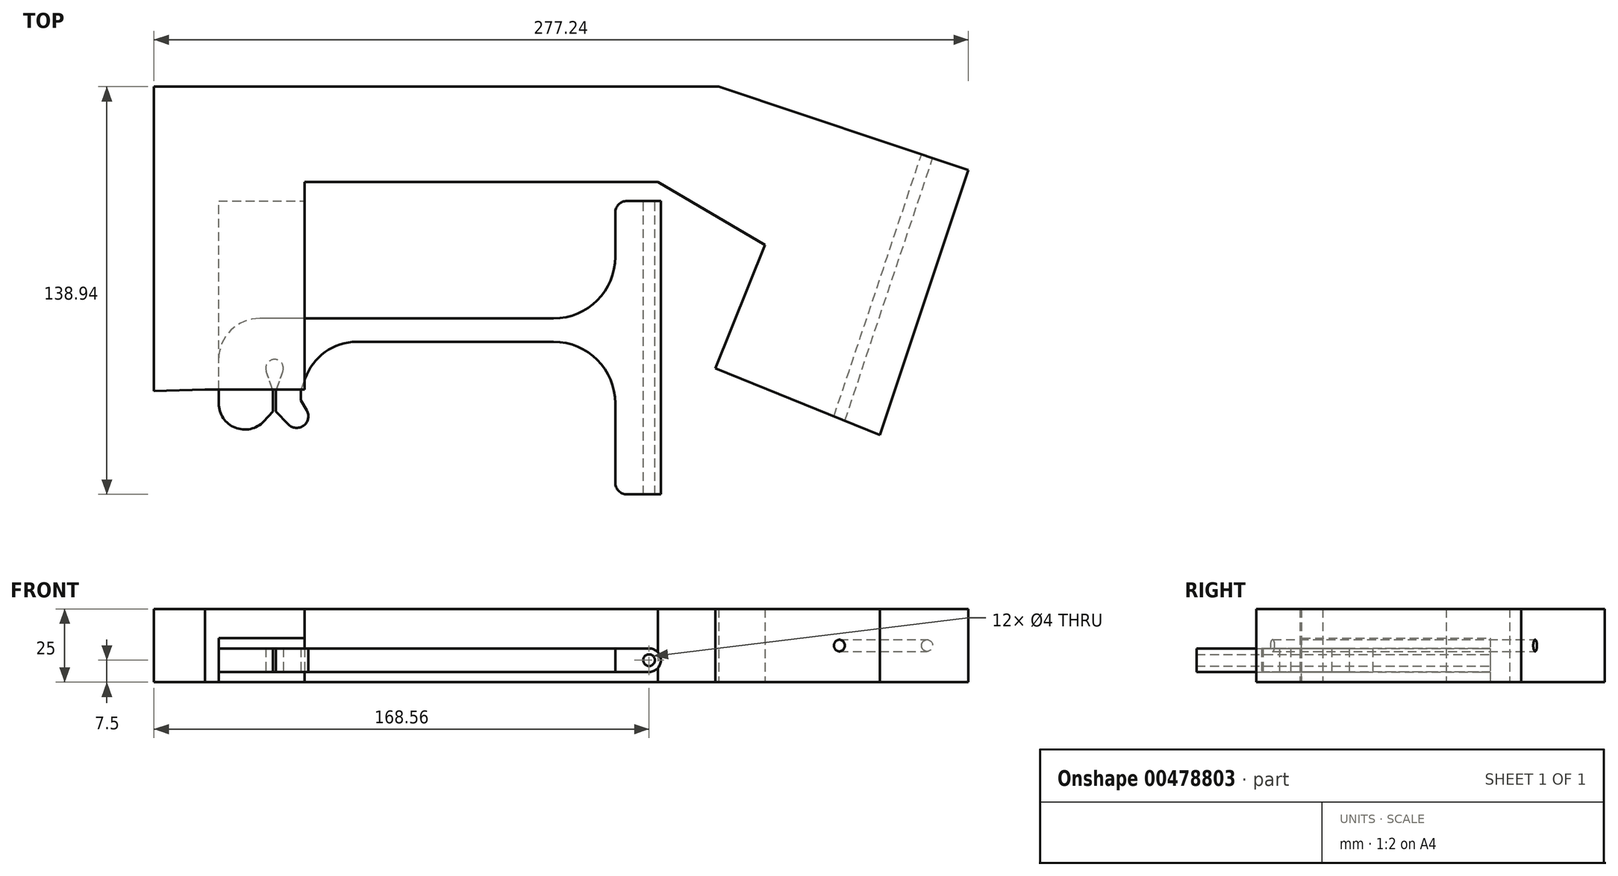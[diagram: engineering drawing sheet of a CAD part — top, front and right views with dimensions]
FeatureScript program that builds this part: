
annotation { "Feature Type Name" : "Feature", "Feature Type Description" : "" }
export const myFeature = defineFeature(function(context is Context, id is Id, definition is map)
    precondition{}
    {
        {
            var Q0;
            Q0=qCreatedBy(makeId("Top.planeOp"),FACE);
            var sketch = newSketch(context, id + "F0", { "sketchPlane" : qUnion([Q0])});
            skLineSegment(sketch, "E0", {"start": v(0, 0) * mm, "end": v(-2.07, 2.07) * mm});
            skLineSegment(sketch, "E1", {"start": v(-7.07, 7.07) * mm, "end": v(-7.07, 27.07) * mm, "construction": true});
            skLineSegment(sketch, "E2", {"start": v(-7.07, 7.07) * mm, "end": v(-12.07, 2.07) * mm, "construction": true});
            skLineSegment(sketch, "E3", {"start": v(-7.07, 27.07) * mm, "end": v(-2.07, 29.96) * mm, "construction": true});
            skLineSegment(sketch, "E4", {"start": v(-7.07, 27.07) * mm, "end": v(-12.07, 29.96) * mm, "construction": true});
            skArc(sketch, "E5", {"start": v(-12.07, 29.96) * mm, "mid": v(-7.07, 48.62) * mm, "end": v(-2.07, 29.96) * mm});
            skLineSegment(sketch, "E6.0", {"start": v(-2.07, 2.07) * mm, "end": v(-2.07, 29.96) * mm});
            skLineSegment(sketch, "E7.0", {"start": v(-12.07, 2.07) * mm, "end": v(-12.07, 29.96) * mm});
            skLineSegment(sketch, "E8", {"start": v(-12.07, 29.96) * mm, "end": v(-12.07, 29.96) * mm});
            skLineSegment(sketch, "E9", {"start": v(-2.07, 29.96) * mm, "end": v(-2.07, 29.96) * mm});
            skLineSegment(sketch, "E10", {"start": v(-12.07, 2.07) * mm, "end": v(-14.14, 0) * mm});
            skLineSegment(sketch, "E11", {"start": v(-2.07, 2.07) * mm, "end": v(-7.07, 7.07) * mm, "construction": true});
            skLineSegment(sketch, "E12", {"start": v(-14.14, 0) * mm, "end": v(-24.14, 0) * mm});
            skLineSegment(sketch, "E13", {"start": v(-24.14, 0) * mm, "end": v(-24.14, 60) * mm});
            skLineSegment(sketch, "E14", {"start": v(-24.14, 60) * mm, "end": v(175.86, 60) * mm});
            skLineSegment(sketch, "E15", {"start": v(175.86, 60) * mm, "end": v(175.86, 0) * mm});
            skLineSegment(sketch, "E16.bottom", {"start": v(-17.07, 48.62) * mm, "end": v(2.93, 48.62) * mm});
            skLineSegment(sketch, "E16.top", {"start": v(-17.07, 28.62) * mm, "end": v(2.93, 28.62) * mm});
            skLineSegment(sketch, "E16.left", {"start": v(-17.07, 48.62) * mm, "end": v(-17.07, 28.62) * mm});
            skLineSegment(sketch, "E16.right", {"start": v(2.93, 48.62) * mm, "end": v(2.93, 28.62) * mm});
            skFitSpline(sketch, "E17", {"points": [v(0, 0) * mm, v(-2.07, 2.07) * mm, v(-2.07, 29.96) * mm, v(2.93, 38.62) * mm, v(2.93, 48.62) * mm, v(-17.07, 48.62) * mm, v(-17.07, 38.62) * mm, v(-12.07, 29.96) * mm, v(-12.07, 2.07) * mm, v(-14.14, 0) * mm, v(-24.14, 60) * mm, v(175.86, 60) * mm, v(175.86, 0) * mm], "startDerivative": vector(-121.96, 63.14) * mm, "endDerivative": vector(-229.47, -514.3) * mm});
            skSolve(sketch);
        }
        {
            var Q0;
            Q0=sQuery(id+"F0.wireOp",EDGE,"E17");
            extrude(context, id + "F1", {"bodyType" : ToolBodyType.SURFACE, "surfaceEntities" : qUnion([Q0]), "depth" : 25 * mm});
        }
        {
            var Q0;
            Q0=qCreatedBy(makeId("Top.planeOp"),FACE);
            var sketch = newSketch(context, id + "F2", { "sketchPlane" : qUnion([Q0])});
            skLineSegment(sketch, "E18", {"start": v(-23.73, -7.24) * mm, "end": v(10.25, -7.24) * mm});
            skLineSegment(sketch, "E19", {"start": v(10.25, -7.24) * mm, "end": v(10.25, 63.52) * mm});
            skLineSegment(sketch, "E20", {"start": v(10.25, 63.52) * mm, "end": v(130.47, 63.52) * mm});
            skLineSegment(sketch, "E21", {"start": v(130.47, 63.52) * mm, "end": v(166.99, 41.96) * mm});
            skLineSegment(sketch, "E22", {"start": v(166.99, 41.96) * mm, "end": v(150, 0) * mm});
            skLineSegment(sketch, "E23", {"start": v(150, 0) * mm, "end": v(206.05, -22.7) * mm});
            skLineSegment(sketch, "E24", {"start": v(206.05, -22.7) * mm, "end": v(236.18, 67.57) * mm});
            skLineSegment(sketch, "E25", {"start": v(236.18, 67.57) * mm, "end": v(151.2, 95.94) * mm});
            skLineSegment(sketch, "E26", {"start": v(151.2, 95.94) * mm, "end": v(-41.06, 95.94) * mm});
            skLineSegment(sketch, "E27", {"start": v(-41.06, 95.94) * mm, "end": v(-41.06, -7.75) * mm});
            skLineSegment(sketch, "E28", {"start": v(-41.06, -7.75) * mm, "end": v(-23.73, -7.24) * mm});
            skSolve(sketch);
        }
        {
            var Q0;
            Q0=makeQuery(id+"F2.imprint","IMPRINT",FACE,{"disambiguationData":[TD([[makeQuery(id+"F2.imprint","IMPRINT",EDGE,{"derivedFrom":sQuery(id+"F2.wireOp",EDGE,"E18")}),1.0]])]});
            extrude(context, id + "F3", {"entities" : qUnion([Q0]), "depth" : 25 * mm});
        }
        {
            var Q0;
            Q0=makeQuery(id+"F3.opExtrude","SWEPT_FACE",FACE,{"disambiguationData":[OSD([sQuery(id+"F2.wireOp",EDGE,"E25")])]});
            var sketch = newSketch(context, id + "F4", { "sketchPlane" : qUnion([Q0])});
            skLineSegment(sketch, "E29.0.0", {"start": v(-202.64, 0) * mm, "end": v(-113.04, 0) * mm});
            skLineSegment(sketch, "E29.0.1", {"start": v(-113.04, 0) * mm, "end": v(-113.04, 25) * mm});
            skLineSegment(sketch, "E29.0.2", {"start": v(-113.04, 25) * mm, "end": v(-202.64, 25) * mm});
            skLineSegment(sketch, "E29.0.3", {"start": v(-202.64, 25) * mm, "end": v(-202.64, 0) * mm});
            skCircle(sketch, "E30", {"center": v(-187.81, 12.5) * mm, "radius": 2 * mm});
            skPoint(sketch, "E30.centerSnap0", {"position": v(-202.64, 12.5) * mm});
            skSolve(sketch);
        }
        {
            var Q0;
            Q0=makeQuery(id+"F4.imprint","IMPRINT",FACE,{"disambiguationData":[TD([[makeQuery(id+"F4.imprint","IMPRINT",EDGE,{"derivedFrom":sQuery(id+"F4.wireOp",EDGE,"E30")}),1.0]])]});
            var Q1;
            Q1=makeQuery(id+"F3.opExtrude","SWEPT_FACE",FACE,{"disambiguationData":[OSD([sQuery(id+"F2.wireOp",EDGE,"E23")])]});
            extrude(context, id + "F5", {"entities" : qUnion([Q0]), "operationType" : NewBodyOperationType.REMOVE, "endBound" : BoundingType.UP_TO_SURFACE, "oppositeDirection" : true, "endBoundEntityFace" : qUnion([Q1]), "depth" : 25 * mm});
        }
        {
            var Q0;
            Q0=qCreatedBy(makeId("Top.planeOp"),FACE);
            var sketch = newSketch(context, id + "F6", { "sketchPlane" : qUnion([Q0])});
            skArc(sketch, "E31", {"start": v(6.62, -2.27) * mm, "mid": v(0, 7) * mm, "end": v(-6.62, -2.27) * mm});
            skLineSegment(sketch, "E32", {"start": v(6.62, -2.27) * mm, "end": v(5, -7) * mm});
            skLineSegment(sketch, "E33", {"start": v(5, -7) * mm, "end": v(5, -12) * mm});
            skLineSegment(sketch, "E34", {"start": v(5, -12) * mm, "end": v(7.5, -16.33) * mm});
            skLineSegment(sketch, "E35.MirrorCS", {"start": v(-6.62, -2.27) * mm, "end": v(-5, -7) * mm});
            skLineSegment(sketch, "E36.MirrorCS", {"start": v(-5, -7) * mm, "end": v(-5, -12) * mm});
            skLineSegment(sketch, "E37.MirrorCS", {"start": v(-5, -12) * mm, "end": v(-7.5, -16.33) * mm});
            skLineSegment(sketch, "E38.2", {"start": v(-2.84, -0.97) * mm, "end": v(-0.5, -7.8) * mm});
            skLineSegment(sketch, "E38.5", {"start": v(2.84, -0.97) * mm, "end": v(0.5, -7.8) * mm});
            skArc(sketch, "E38.6", {"start": v(2.84, -0.97) * mm, "mid": v(0, 3) * mm, "end": v(-2.84, -0.97) * mm});
            skArc(sketch, "E39", {"start": v(-10.96, -14.33) * mm, "mid": v(-9.9, -19.53) * mm, "end": v(-4.6, -19.09) * mm, "construction": true});
            skArc(sketch, "E40.MirrorCS", {"start": v(10.96, -14.33) * mm, "mid": v(9.9, -19.53) * mm, "end": v(4.6, -19.09) * mm});
            skLineSegment(sketch, "E41.0", {"start": v(9, -10.93) * mm, "end": v(10.96, -14.33) * mm});
            skLineSegment(sketch, "E41.1", {"start": v(9, -7.67) * mm, "end": v(9, -10.93) * mm});
            skLineSegment(sketch, "E41.2", {"start": v(10.4, -3.57) * mm, "end": v(9, -7.67) * mm});
            skLineSegment(sketch, "E41.3", {"start": v(-9, -10.93) * mm, "end": v(-10.96, -14.33) * mm, "construction": true});
            skLineSegment(sketch, "E41.4", {"start": v(-9, -7.67) * mm, "end": v(-9, -10.93) * mm, "construction": true});
            skLineSegment(sketch, "E41.5", {"start": v(-10.4, -3.57) * mm, "end": v(-9, -7.67) * mm, "construction": true});
            skArc(sketch, "E41.6", {"start": v(10.4, -3.57) * mm, "mid": v(0, 11) * mm, "end": v(-10.4, -3.57) * mm, "construction": true});
            skPoint(sketch, "E42.orphan", {"position": v(-5.5, -12.87) * mm});
            skPoint(sketch, "E43.orphan", {"position": v(5.5, -12.87) * mm});
            skLineSegment(sketch, "E44", {"start": v(0, 0) * mm, "end": v(0, -13.5) * mm, "construction": true});
            skLineSegment(sketch, "E45", {"start": v(0, -9.25) * mm, "end": v(0, -14.25) * mm, "construction": true});
            skLineSegment(sketch, "E46", {"start": v(0, -14.25) * mm, "end": v(-0.5, -14.78) * mm, "construction": true});
            skLineSegment(sketch, "E47", {"start": v(0, -14.25) * mm, "end": v(0.5, -14.78) * mm, "construction": true});
            skLineSegment(sketch, "E48", {"start": v(-7.5, -16.33) * mm, "end": v(-12.5, -16.33) * mm});
            skLineSegment(sketch, "E49", {"start": v(-12.5, -16.33) * mm, "end": v(-15, -12) * mm});
            skLineSegment(sketch, "E50", {"start": v(-15, -12) * mm, "end": v(-15, 3) * mm});
            skArc(sketch, "E51", {"start": v(-15, 3) * mm, "mid": v(-12.07, 10.07) * mm, "end": v(-5, 13) * mm});
            skLineSegment(sketch, "E52", {"start": v(-5, 13) * mm, "end": v(95, 13) * mm});
            skArc(sketch, "E53", {"start": v(95, 13) * mm, "mid": v(112.68, 5.68) * mm, "end": v(120, -12) * mm});
            skLineSegment(sketch, "E54", {"start": v(120, -12) * mm, "end": v(120, -39) * mm});
            skLineSegment(sketch, "E55.0", {"start": v(124, -12) * mm, "end": v(124, -39) * mm});
            skLineSegment(sketch, "E55.1", {"start": v(-19, -12) * mm, "end": v(-19, 3) * mm});
            skArc(sketch, "E55.2", {"start": v(-19, 3) * mm, "mid": v(-14.9, 12.9) * mm, "end": v(-5, 17) * mm});
            skLineSegment(sketch, "E55.3", {"start": v(-5, 17) * mm, "end": v(95, 17) * mm});
            skArc(sketch, "E55.4", {"start": v(95, 17) * mm, "mid": v(115.5, 8.5) * mm, "end": v(124, -12) * mm});
            skLineSegment(sketch, "E56.0", {"start": v(116, -12) * mm, "end": v(116, -39) * mm});
            skArc(sketch, "E56.1", {"start": v(95, 9) * mm, "mid": v(109.85, 2.85) * mm, "end": v(116, -12) * mm});
            skLineSegment(sketch, "E56.2", {"start": v(-5, 9) * mm, "end": v(95, 9) * mm});
            skArc(sketch, "E57", {"start": v(116, -39) * mm, "mid": v(120, -43) * mm, "end": v(124, -39) * mm});
            skLineSegment(sketch, "E58", {"start": v(120, -43) * mm, "end": v(135, -43) * mm});
            skPoint(sketch, "E58.endSnap0", {"position": v(120, -43) * mm});
            skLineSegment(sketch, "E59", {"start": v(135, -43) * mm, "end": v(135, 17) * mm});
            skLineSegment(sketch, "E60", {"start": v(135, 17) * mm, "end": v(124, 17) * mm});
            skLineSegment(sketch, "E61", {"start": v(124, 17) * mm, "end": v(95, 17) * mm});
            skArc(sketch, "E62", {"start": v(-19, -12) * mm, "mid": v(-13.41, -20.25) * mm, "end": v(-3.68, -18.12) * mm});
            skLineSegment(sketch, "E63", {"start": v(-3.68, -18.12) * mm, "end": v(-4.6, -19.09) * mm, "construction": true});
            skArc(sketch, "E64", {"start": v(28, 9) * mm, "mid": v(17.19, 5.54) * mm, "end": v(10.4, -3.57) * mm});
            skLineSegment(sketch, "E65", {"start": v(-0.5, -14.78) * mm, "end": v(-0.5, -7.8) * mm});
            skLineSegment(sketch, "E66.MirrorCS", {"start": v(0.5, -14.78) * mm, "end": v(0.5, -7.8) * mm});
            skLineSegment(sketch, "E67", {"start": v(-0.5, -7.8) * mm, "end": v(0, -9.25) * mm, "construction": true});
            skLineSegment(sketch, "E68", {"start": v(0.5, -7.8) * mm, "end": v(0, -9.25) * mm, "construction": true});
            skLineSegment(sketch, "E69", {"start": v(-0.5, -14.78) * mm, "end": v(-3.68, -18.12) * mm});
            skLineSegment(sketch, "E70", {"start": v(0.5, -14.78) * mm, "end": v(4.6, -19.09) * mm});
            skArc(sketch, "E71", {"start": v(95, 13) * mm, "mid": v(112.68, 20.32) * mm, "end": v(120, 38) * mm});
            skArc(sketch, "E72.0", {"start": v(95, 17) * mm, "mid": v(109.85, 23.15) * mm, "end": v(116, 38) * mm});
            skLineSegment(sketch, "E73", {"start": v(135, 17) * mm, "end": v(135, 57) * mm});
            skArc(sketch, "E74", {"start": v(120, 57) * mm, "mid": v(117.17, 55.83) * mm, "end": v(116, 53) * mm});
            skLineSegment(sketch, "E75", {"start": v(116, 38) * mm, "end": v(116, 53) * mm});
            skLineSegment(sketch, "E76", {"start": v(120, 57) * mm, "end": v(135, 57) * mm});
            skSolve(sketch);
        }
        {
            var Q0;
            {var subQ1=sQuery(id+"F6.wireOp",EDGE,"E55.0");Q0=makeQuery(id+"F6.imprint","IMPRINT",FACE,{"disambiguationData":[TD([[makeQuery(id+"F6.imprint","IMPRINT",EDGE,{"derivedFrom":subQ1}),1.0]])]});}
            var Q1;
            Q1=makeQuery(id+"F6.imprint","IMPRINT",FACE,{"disambiguationData":[TD([[makeQuery(id+"F6.imprint","IMPRINT",EDGE,{"derivedFrom":sQuery(id+"F6.wireOp",EDGE,"E38.2")}),-1.0]])]});
            var Q2;
            {var subQ3=sQuery(id+"F6.wireOp",EDGE,"E60");Q2=makeQuery(id+"F6.imprint","IMPRINT",FACE,{"disambiguationData":[TD([[makeQuery(id+"F6.imprint","IMPRINT",EDGE,{"derivedFrom":subQ3}),-1.0]])]});}
            var Q3;
            {var subQ1=sQuery(id+"F6.wireOp",EDGE,"E55.4");var subQ3=sQuery(id+"F6.wireOp",EDGE,"E71");var subQ4=makeQuery(id+"F6.imprint","INTERSECT",VERTEX,{"derivedFrom":[subQ1,subQ3]});Q3=makeQuery(id+"F6.imprint","IMPRINT",FACE,{"disambiguationData":[TD([[makeQuery(id+"F6.imprint","IMPRINT",EDGE,{"disambiguationData":[TD([[subQ4,-1.0]])],"derivedFrom":subQ3}),1.0]])]});}
            extrude(context, id + "F7", {"entities" : qUnion([Q0, Q1, Q2, Q3]), "depth" : 15 * mm});
        }
        {
            var Q0;
            Q0=makeQuery(id+"F7.opExtrude","SWEPT_FACE",FACE,{"disambiguationData":[OSD([sQuery(id+"F6.wireOp",EDGE,"E76")])]});
            var sketch = newSketch(context, id + "F8", { "sketchPlane" : qUnion([Q0])});
            skLineSegment(sketch, "E77.0.0", {"start": v(-120, 0) * mm, "end": v(-135, 0) * mm});
            skLineSegment(sketch, "E77.0.1", {"start": v(-135, 0) * mm, "end": v(-135, 15) * mm});
            skLineSegment(sketch, "E77.0.2", {"start": v(-135, 15) * mm, "end": v(-120, 15) * mm});
            skLineSegment(sketch, "E77.0.3", {"start": v(-120, 15) * mm, "end": v(-120, 0) * mm});
            skCircle(sketch, "E78", {"center": v(-127.5, 7.5) * mm, "radius": 2 * mm});
            skLineSegment(sketch, "E79", {"start": v(-127.5, 7.5) * mm, "end": v(-127.5, 15) * mm, "construction": true});
            skLineSegment(sketch, "E80", {"start": v(-127.5, 7.5) * mm, "end": v(-135, 7.5) * mm, "construction": true});
            skSolve(sketch);
        }
        {
            var Q0;
            Q0=makeQuery(id+"F8.imprint","IMPRINT",FACE,{"disambiguationData":[TD([[makeQuery(id+"F8.imprint","IMPRINT",EDGE,{"derivedFrom":sQuery(id+"F8.wireOp",EDGE,"E78")}),1.0]])]});
            extrude(context, id + "F9", {"entities" : qUnion([Q0]), "operationType" : NewBodyOperationType.REMOVE, "endBound" : BoundingType.THROUGH_ALL, "oppositeDirection" : true, "depth" : 25 * mm});
        }
        {
            var Q0;
            Q0=makeQuery(id+"F7.opExtrude","SWEPT_FACE",FACE,{"disambiguationData":[OSD([sQuery(id+"F6.wireOp",EDGE,"E76")])]});
            var sketch = newSketch(context, id + "F10", { "sketchPlane" : qUnion([Q0])});
            skCircle(sketch, "E81", {"center": v(-127.5, 7.5) * mm, "radius": 4 * mm});
            skLineSegment(sketch, "E82.0.0", {"start": v(-95, 0) * mm, "end": v(5, 0) * mm});
            skLineSegment(sketch, "E82.0.1", {"start": v(5, 0) * mm, "end": v(5, 15) * mm});
            skLineSegment(sketch, "E82.0.2", {"start": v(5, 15) * mm, "end": v(-95, 15) * mm});
            skLineSegment(sketch, "E82.0.3", {"start": v(-95, 15) * mm, "end": v(-95, 0) * mm});
            skLineSegment(sketch, "E83.0.0", {"start": v(5, 0) * mm, "end": v(19, 0) * mm});
            skLineSegment(sketch, "E83.0.1", {"start": v(19, 0) * mm, "end": v(19, 15) * mm});
            skLineSegment(sketch, "E83.0.2", {"start": v(19, 15) * mm, "end": v(5, 15) * mm});
            skLineSegment(sketch, "E83.0.3", {"start": v(5, 15) * mm, "end": v(5, 0) * mm});
            skLineSegment(sketch, "E84.0.0", {"start": v(-116, 0) * mm, "end": v(-95, 0) * mm});
            skLineSegment(sketch, "E84.0.1", {"start": v(-95, 0) * mm, "end": v(-95, 15) * mm});
            skLineSegment(sketch, "E84.0.2", {"start": v(-95, 15) * mm, "end": v(-116, 15) * mm});
            skLineSegment(sketch, "E84.0.3", {"start": v(-116, 15) * mm, "end": v(-116, 0) * mm});
            skLineSegment(sketch, "E85.0.1", {"start": v(-116, 0) * mm, "end": v(-116, 15) * mm});
            skCircle(sketch, "E86.0", {"center": v(-127.5, 7.5) * mm, "radius": 2 * mm});
            skLineSegment(sketch, "E87.0.0", {"start": v(-135, 0) * mm, "end": v(-120, 0) * mm});
            skLineSegment(sketch, "E87.0.1", {"start": v(-120, 0) * mm, "end": v(-120, 15) * mm});
            skLineSegment(sketch, "E87.0.2", {"start": v(-120, 15) * mm, "end": v(-135, 15) * mm});
            skLineSegment(sketch, "E87.0.3", {"start": v(-135, 15) * mm, "end": v(-135, 0) * mm});
            skLineSegment(sketch, "E88.0.0", {"start": v(-120, 0) * mm, "end": v(-116, 0) * mm});
            skLineSegment(sketch, "E88.0.2", {"start": v(-116, 15) * mm, "end": v(-120, 15) * mm});
            skLineSegment(sketch, "E88.0.3", {"start": v(-120, 15) * mm, "end": v(-120, 0) * mm});
            skLineSegment(sketch, "E89", {"start": v(-127.5, 11.5) * mm, "end": v(19, 11.5) * mm});
            skPoint(sketch, "E89.startSnap0", {"position": v(-127.5, 15) * mm});
            skLineSegment(sketch, "E90", {"start": v(-127.5, 3.5) * mm, "end": v(19, 3.5) * mm});
            skSolve(sketch);
        }
        {
            var Q0;
            {var subQ5=sQuery(id+"F10.wireOp",EDGE,"E87.0.0");Q0=makeQuery(id+"F10.imprint","IMPRINT",FACE,{"disambiguationData":[TD([[makeQuery(id+"F10.imprint","IMPRINT",EDGE,{"derivedFrom":subQ5}),-1.0]])]});}
            var Q1;
            {var subQ5=sQuery(id+"F10.wireOp",EDGE,"E88.0.2");Q1=makeQuery(id+"F10.imprint","IMPRINT",FACE,{"disambiguationData":[TD([[makeQuery(id+"F10.imprint","IMPRINT",EDGE,{"derivedFrom":subQ5}),1.0]])]});}
            var Q2;
            {var subQ0=sQuery(id+"F10.wireOp",EDGE,"E84.0.2");Q2=makeQuery(id+"F10.imprint","IMPRINT",FACE,{"disambiguationData":[TD([[makeQuery(id+"F10.imprint","IMPRINT",EDGE,{"derivedFrom":subQ0}),1.0]])]});}
            var Q3;
            {var subQ5=sQuery(id+"F10.wireOp",EDGE,"E88.0.0");Q3=makeQuery(id+"F10.imprint","IMPRINT",FACE,{"disambiguationData":[TD([[makeQuery(id+"F10.imprint","IMPRINT",EDGE,{"derivedFrom":subQ5}),1.0]])]});}
            var Q4;
            {var subQ0=sQuery(id+"F10.wireOp",EDGE,"E84.0.0");Q4=makeQuery(id+"F10.imprint","IMPRINT",FACE,{"disambiguationData":[TD([[makeQuery(id+"F10.imprint","IMPRINT",EDGE,{"derivedFrom":subQ0}),1.0]])]});}
            var Q5;
            {var subQ0=sQuery(id+"F10.wireOp",EDGE,"E82.0.0");Q5=makeQuery(id+"F10.imprint","IMPRINT",FACE,{"disambiguationData":[TD([[makeQuery(id+"F10.imprint","IMPRINT",EDGE,{"derivedFrom":subQ0}),1.0]])]});}
            var Q6;
            {var subQ0=sQuery(id+"F10.wireOp",EDGE,"E82.0.2");Q6=makeQuery(id+"F10.imprint","IMPRINT",FACE,{"disambiguationData":[TD([[makeQuery(id+"F10.imprint","IMPRINT",EDGE,{"derivedFrom":subQ0}),1.0]])]});}
            var Q7;
            {var subQ0=sQuery(id+"F10.wireOp",EDGE,"E83.0.2");Q7=makeQuery(id+"F10.imprint","IMPRINT",FACE,{"disambiguationData":[TD([[makeQuery(id+"F10.imprint","IMPRINT",EDGE,{"derivedFrom":subQ0}),1.0]])]});}
            var Q8;
            {var subQ0=sQuery(id+"F10.wireOp",EDGE,"E83.0.0");Q8=makeQuery(id+"F10.imprint","IMPRINT",FACE,{"disambiguationData":[TD([[makeQuery(id+"F10.imprint","IMPRINT",EDGE,{"derivedFrom":subQ0}),1.0]])]});}
            extrude(context, id + "F11", {"entities" : qUnion([Q0, Q1, Q2, Q3, Q4, Q5, Q6, Q7, Q8]), "operationType" : NewBodyOperationType.REMOVE, "endBound" : BoundingType.THROUGH_ALL, "oppositeDirection" : true, "depth" : 25 * mm});
        }
    });
